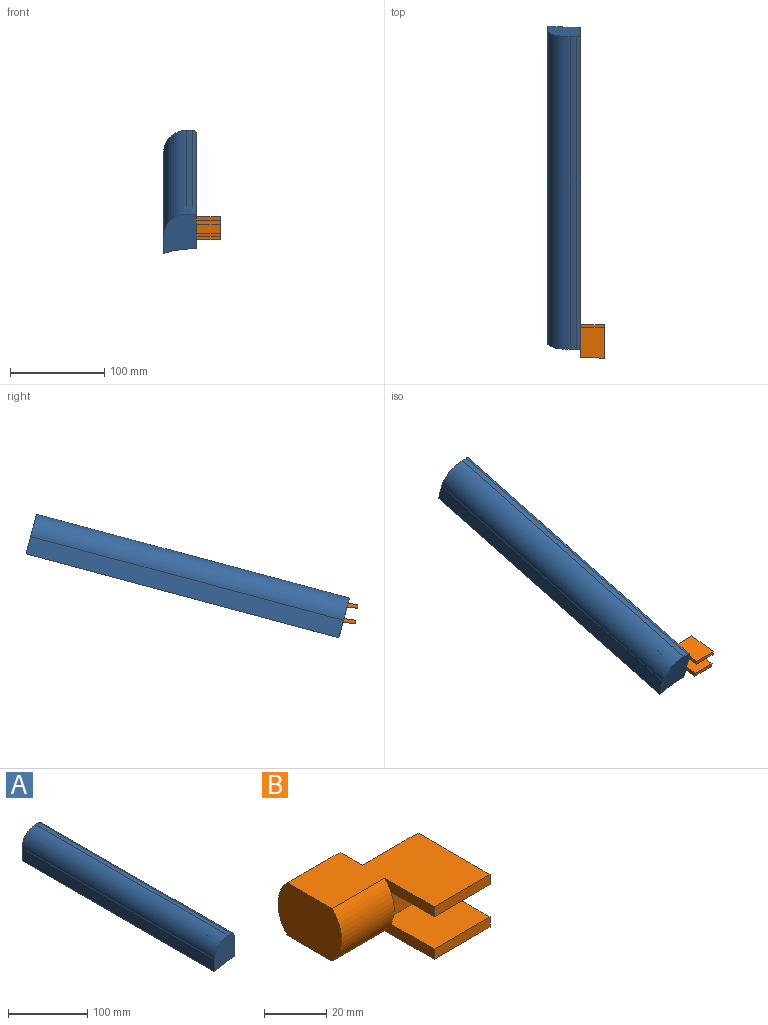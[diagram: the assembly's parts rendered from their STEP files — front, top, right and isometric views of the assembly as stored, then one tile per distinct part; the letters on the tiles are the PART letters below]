
ASSEMBLY  parts=2 mates=2
PART A: 15 faces, bbox 34.7x342.9x43.5 mm
  f0: plane 23.93x20.68mm, normal (0,-1,0), area 495mm2, adj f1,f8,f9,f10
  f1: plane 342.9x33.19mm, normal (1,0,0), area 4479.6mm2, adj f0,f2,f6,f7,f8,f10,f11,f12
  f2: cylinder r=4.47mm len=342.9mm, axis (0,1,0), area 2409.9mm2, adj f1,f3,f7,f11,f13
  f3: plane 342.9x5.87mm, normal (0,0,1), area 2011.5mm2, adj f2,f4,f7,f11
  f4: cylinder r=24.4mm len=342.9mm, axis (0,1,0), area 13144.2mm2, adj f3,f5,f7,f11
  f5: plane 342.9x19.1mm, normal (-1,0,0), area 6549.2mm2, adj f4,f6,f7,f11
  f6: extruded ~342.9x34.74mm, area 12151.5mm2, adj f1,f5,f7,f11
  f7: plane 43.5x34.74mm, normal (0,1,0), area 1241.9mm2, adj f1,f2,f3,f4,f5,f6
  f8: plane 304.8x23.93mm, normal (0,0,1), area 7295mm2, adj f0,f1,f9,f14
  f9: plane 329.41x28.9mm, normal (1,0,0), area 6901mm2, adj f0,f8,f10,f12,f13,f14
  f10: plane 304.8x23.93mm, normal (0,0,-1), area 7295mm2, adj f0,f1,f9,f12
  f11: plane 43.5x34.74mm, normal (0,-1,0), area 1241.9mm2, adj f1,f2,f3,f4,f5,f6
  f12: cylinder r=14.48mm len=23.93mm, axis (1,0,0), area 238.4mm2, adj f1,f9,f10,f13
  f13: plane 23.93x2.52mm, normal (0,0,-1), area 60.3mm2, adj f2,f9,f12,f14
  f14: cylinder r=14.48mm len=28.9mm, axis (1,0,0), area 1327.1mm2, adj f1,f8,f9,f13
PART B: 16 faces, bbox 49.3x47.2x20.7 mm
  f0: plane 20.68x14.48mm, normal (1,0,0), area 271.6mm2, adj f2,f3,f4,f14
  f1: plane 12.73x4.35mm, normal (1,0,0), area 49.2mm2, adj f5,f10,f11,f12
  f2: plane 49.33x42.86mm, normal (0,0,-1), area 1316.3mm2, adj f0,f3,f5,f6,f8,f13,f14,f15
  f3: cylinder r=14.48mm len=23.93mm, axis (-1,0,0), area 551.4mm2, adj f0,f2,f4,f6
  f4: plane 49.33x42.86mm, normal (0,0,1), area 1316.3mm2, adj f0,f3,f5,f6,f7,f9,f14,f15
  f5: cylinder r=14.48mm len=23.93mm, axis (-1,0,0), area 551.4mm2, adj f1,f2,f4,f6,f7,f8
  f6: plane 28.96x20.68mm, normal (-1,0,0), area 543.2mm2, adj f2,f3,f4,f5
  f7: plane 22.59x3.98mm, normal (-1,0,0), area 83.4mm2, adj f4,f5,f9,f10
  f8: plane 22.59x3.98mm, normal (-1,0,0), area 83.4mm2, adj f2,f5,f12,f13
  f9: plane 25.4x3.98mm, normal (0,-1,0), area 101mm2, adj f4,f7,f10,f15
  f10: plane 25.4x22.59mm, normal (0,0,-1), area 573.8mm2, adj f1,f7,f9,f11,f15
  f11: plane 25.4x12.73mm, normal (0,-1,0), area 323.4mm2, adj f1,f10,f12,f15
  f12: plane 25.4x22.59mm, normal (0,0,1), area 573.8mm2, adj f1,f8,f11,f13,f15
  f13: plane 25.4x3.98mm, normal (0,-1,0), area 101mm2, adj f2,f8,f12,f15
  f14: plane 25.4x20.68mm, normal (0,1,0), area 525.4mm2, adj f0,f2,f4,f15
  f15: plane 32.73x20.68mm, normal (1,0,0), area 389.3mm2, adj f2,f4,f9,f10,f11,f12,f13,f14
PLACE A rot(axis=(1,0,0),15deg) t=(18.33,6.35,100.76)mm fixed
PLACE B rot(axis=(1,0,0),7.4deg) t=(18.33,20.37,-5.13)mm
MATE pin_slot B.f3 <-> A.f12  axis (-1,0,0) through (-141.07,-313.26,48.3)mm
MATE planar B.f3 <-> A.f9  axis (-1,0,0) through (-141.07,-313.26,48.3)mm
